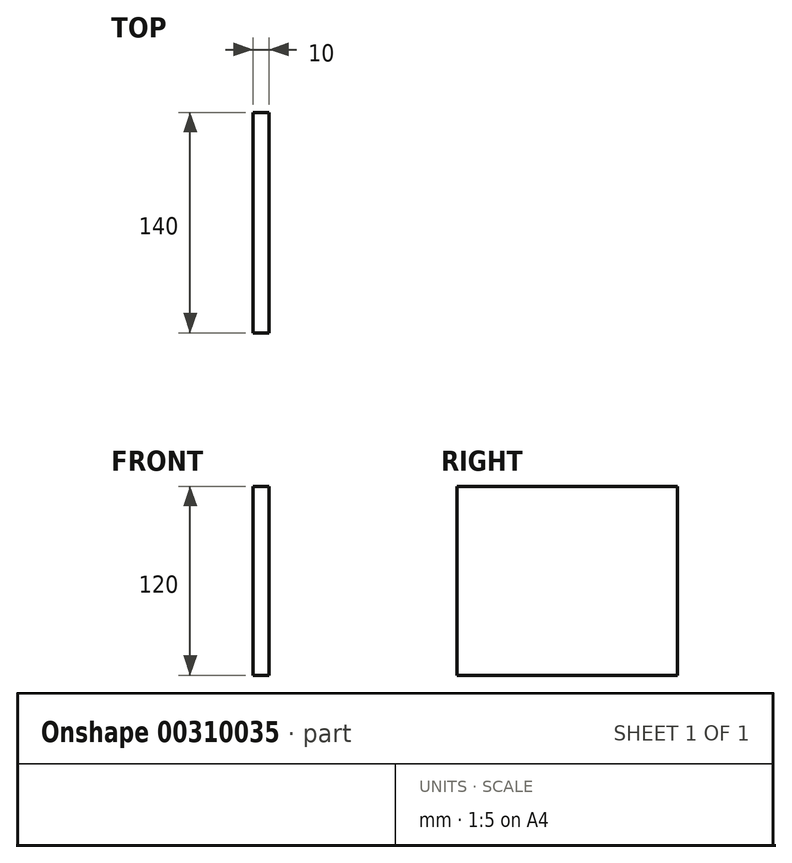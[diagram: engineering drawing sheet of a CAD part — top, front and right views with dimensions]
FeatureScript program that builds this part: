
annotation { "Feature Type Name" : "Feature", "Feature Type Description" : "" }
export const myFeature = defineFeature(function(context is Context, id is Id, definition is map)
    precondition{}
    {
        {
            var Q0;
            Q0=qCreatedBy(makeId("Front.planeOp"),FACE);
            var sketch = newSketch(context, id + "F0", { "sketchPlane" : qUnion([Q0])});
            skLineSegment(sketch, "E0.bottom", {"start": v(-14.46, 123.97) * mm, "end": v(-4.46, 123.97) * mm});
            skLineSegment(sketch, "E0.top", {"start": v(-14.46, 3.97) * mm, "end": v(-4.46, 3.97) * mm});
            skLineSegment(sketch, "E0.left", {"start": v(-14.46, 123.97) * mm, "end": v(-14.46, 3.97) * mm});
            skLineSegment(sketch, "E0.right", {"start": v(-4.46, 123.97) * mm, "end": v(-4.46, 3.97) * mm});
            skSolve(sketch);
        }
        {
            var Q0;
            Q0=qSketchRegion(id+"F0",true);
            extrude(context, id + "F1", {"entities" : qUnion([Q0]), "depth" : 140 * mm});
        }
    });
